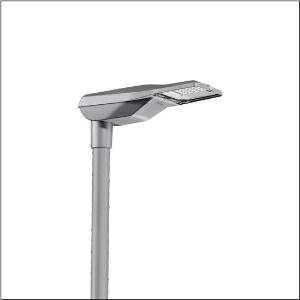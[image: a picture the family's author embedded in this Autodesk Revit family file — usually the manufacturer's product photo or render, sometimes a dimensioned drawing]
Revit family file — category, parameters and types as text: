
# Revit family: streetlight_sl_21_iq_micro___st1_0a_5xe1d61g08cb_d415
name_source: partatom
category: Lighting Fixtures
units: mm (PartAtom-declared; Revit-internal decimal feet)

## family parameters
Cut with Voids When Loaded = No
Host = Face
Light Source = No
Part Type = Normal
Room Calculation Point = No
Round Connector Dimension = Use Diameter
Shared = No

## types (1)
- --- (1 x LED, 2570 lm, 19.4 W, 2700K)
    Apparent Load = 19 VA
    CIE Flux Codes = 37 72 97 100 100
    Color Rendering = 70
    Color Temperature = 2700K
    Default Elevation = 1800 mm
    Description = Streetlight SL 21 iQ micro, mast luminaire, primary light control with lens, of PMMA, primary optical cover: cover, of toughened safety glass, transparent, light distribution: ST1.0a, light emission: direct distribution, primary light characteristic: asymmetric, installation type: post-top, side-entry, LED, High Power LED, rated luminous flux: 2.570lm, luminous efficacy: 133lm/W, light colour: 727, colour temperature: 2700K, control: Street-Remote, Auto-Match, Temp-Guard, Lumen-Switch, Night-Set, Smart-Wire, Light-Fading, Desk-Remote (wireless, voltage-free reading and setting of iQ features in the workshop via application-optimized NFC function/RFID function), optimised constant luminous flux control (CLO 2.0), presetting dimming linear, mains connection: 220..240V, AC, 50/60Hz, start of lifetime: 19W, end of service life: 20W, reduction: 10W, luminaire housing, of diecast aluminium, powder-coated, Siteco® metallic grey (DB 702S), corrosivity category C5 mid according to DIN EN ISO 12944, please order mast flange separately, inclination adjustable: 0°, 5°, 10°, 15°, sealing non-destructively replaceable, multi-level sealing system, length: 528mm, width: 235mm, height: 110mm, mast flange for spigot size: 42mm (side-entry): 5XC10008XM4, 60/48mm (side-entry/post-top): 5XC10108XM2, 76/60mm (side-entry/post-top): 5XC10108XM1, protection rating (complete): IP66, insulation class (complete): insulation class II (safety insulation), certification: CE, ENEC, ENEC+, VDE, impact resistance: IK09, permissible operating ambient temperature for outdoor applications: -40..+50°C, standard-compliant lighting for roads and squares, packaging unit: 1 piece

Light Distribution: ST1.0a
    Height = 110 mm
    Lamp = 1 x LED
    Lamp Light Flux = 2570 lm
    Lamp Power = 19.4 W
    Lamp count = 1
    Length = 528 mm
    Luminous efficacy = 132 lm/W
    Manufacturer = Siteco
    ModVariant = No
    Model = 5XE1D61G08CB
    Number of Poles = 1
    OnlyDefault = Yes
    Power Factor = 1
    Product Name = Streetlight SL 21 iQ micro | ST1.0a
    Product group = mast luminaire | pylon top
    ProductGroupID = 6100
    Protection Class = Protection class II
    Protection Degree = IP 66
    RLX_Detail_Level = 1
    RLX_Emergency_Light_Flux = 0 lm
    RLX_Emergency_Type = 0
    RLX_Emergency_Type_DB = No
    RlxData = <blob elided: 98781 chars, md5=8111f5e1>
    Socket = socket
    Standby Power = 0 W
    System Light Flux = 2570 lm
    System Power = 19 W
    Type Comments = factory setting: luminous flux: 100 % | dim-lin: 254 | 387 mA
    Type Image = l_1006881.jpg
    URL = http://relux.com
    VarID = @adj_088477
    Voltage = 0 V
    Weight = 0.00 kg
    Width = 235 mm

## geometry (parser evidence)
native form markers: Blend x4, Sweep x9
no freeform markers — native parametric forms only
